# Revit family: Toilet_Tissue_Holder-Bradley_Corp-Security-Recessed-SA11
name_source: partatom
category: Specialty Equipment
revit_build: Autodesk Revit MEP 2012 (Build: 20110309_2315(x64)
units: mm (PartAtom-declared; Revit-internal decimal feet)

## types (1)
- SA11
    ADA Compliant = Yes
    Assembly Code = C1030200
    Buy American Act = Yes
    Default Elevation = 48 "
    Depth = 4.313 "
    Description = Security Toilet Tissue Roll Holder
    Height = 6.5 "
    Low Emitting Finish = No
    Low Emitting Material = No
    Manufacturer = Bradley Corporation
    MasterFormat Number = 10 28 13.53
    MasterFormat Title = Security Toilet Accessories
    Material = Metal - Bradley Corp - Stainless Steel - Satin
    Model = SA11
    OmniClass Table 21 Number = 21-03 10 90 40
    OmniClass Table 21 Title = Toilet, Bath, and Laundry Accessories
    OmniClass Table 23 Number = 23.21.43.15.31
    OmniClass Table 23 Title = Toilet Tissue Dispensers
    Percentage of Recycled Content = 0
    Product Tech Data URL - English = http://bradleycorp.com
    Specifications URL = http://www.bradleycorp.com
    URL = http://www.bradleycorp.com
    Version = 2.0
    Warranty Information = Complete Unit - One Year
    Width = 6.5 "

## geometry (parser evidence)
native form markers: Blend x4, Sweep x1
no freeform markers — native parametric forms only
